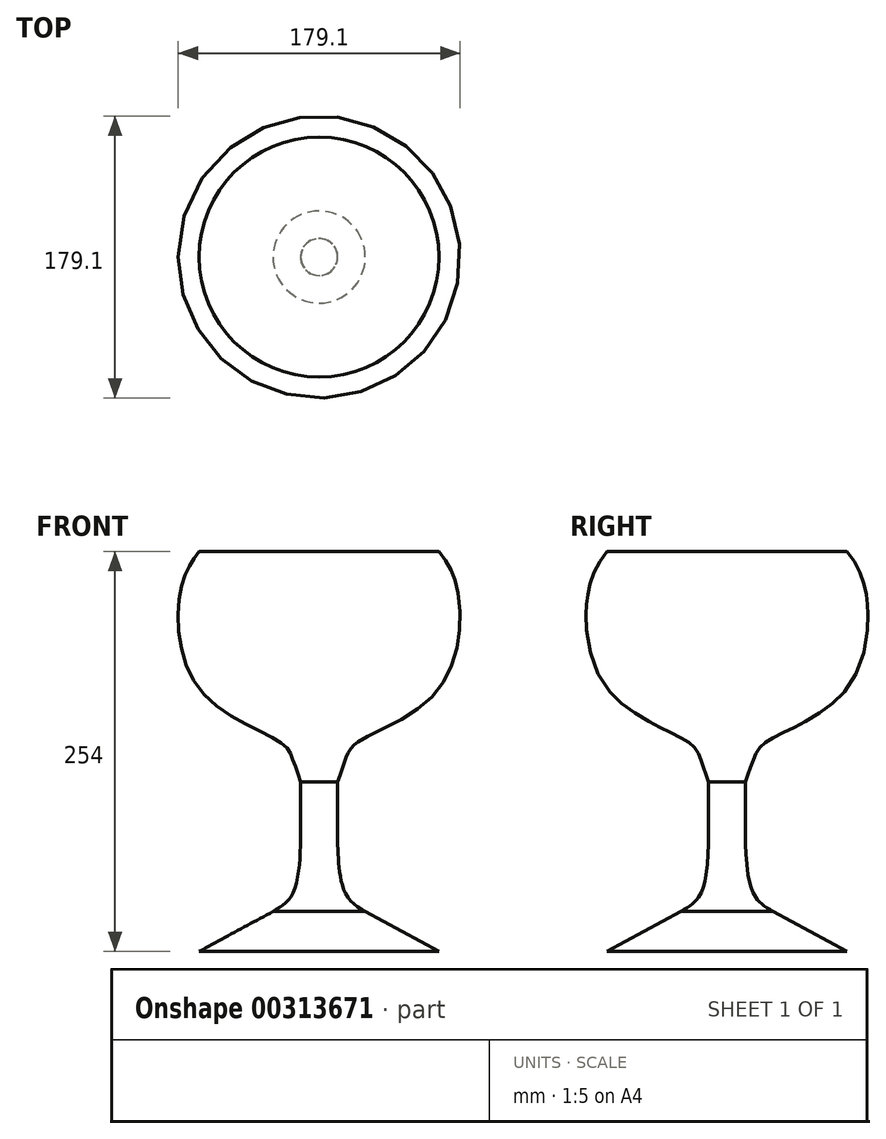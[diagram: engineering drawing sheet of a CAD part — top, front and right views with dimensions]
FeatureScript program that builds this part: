
annotation { "Feature Type Name" : "Feature", "Feature Type Description" : "" }
export const myFeature = defineFeature(function(context is Context, id is Id, definition is map)
    precondition{}
    {
        {
            var Q0;
            Q0=qCreatedBy(makeId("Front.planeOp"),FACE);
            var sketch = newSketch(context, id + "F0", { "sketchPlane" : qUnion([Q0])});
            skLineSegment(sketch, "E0", {"start": v(0, 0) * mm, "end": v(0, 254) * mm});
            skLineSegment(sketch, "E1", {"start": v(0, 0) * mm, "end": v(-76.2, 0) * mm});
            skLineSegment(sketch, "E2", {"start": v(-76.2, 0) * mm, "end": v(-29.28, 25.4) * mm});
            skFitSpline(sketch, "E3", {"points": [v(-29.28, 25.4) * mm, v(-15.9, 38.73) * mm, v(-11.79, 77.6) * mm, v(-11.79, 84.93) * mm], "startDerivative": vector(47.6, 27.5) * mm, "endDerivative": vector(0.12, 26.04) * mm});
            skLineSegment(sketch, "E4", {"start": v(-11.79, 84.93) * mm, "end": v(-11.79, 107.74) * mm});
            skLineSegment(sketch, "E5", {"start": v(0, 254) * mm, "end": v(-76.2, 254) * mm});
            skFitSpline(sketch, "E6", {"points": [v(-76.2, 254) * mm, v(-87.34, 232.29) * mm, v(-76.2, 166.96) * mm, v(-24.45, 132.77) * mm, v(-17.12, 123) * mm, v(-11.79, 107.74) * mm], "startDerivative": vector(-74.44, -98.77) * mm, "endDerivative": vector(39.13, -116.36) * mm});
            skSolve(sketch);
        }
        {
            var Q0;
            Q0=makeQuery(id+"F0.imprint","IMPRINT",FACE,{"disambiguationData":[TD([[makeQuery(id+"F0.imprint","IMPRINT",EDGE,{"derivedFrom":sQuery(id+"F0.wireOp",EDGE,"E0")}),1.0]])]});
            var Q1;
            Q1=sQuery(id+"F0.wireOp",EDGE,"E0");
            revolve(context, id + "F1", {"entities" : qUnion([Q0]), "axis" : qUnion([Q1]), "revolveType" : RevolveType.FULL});
        }
    });
